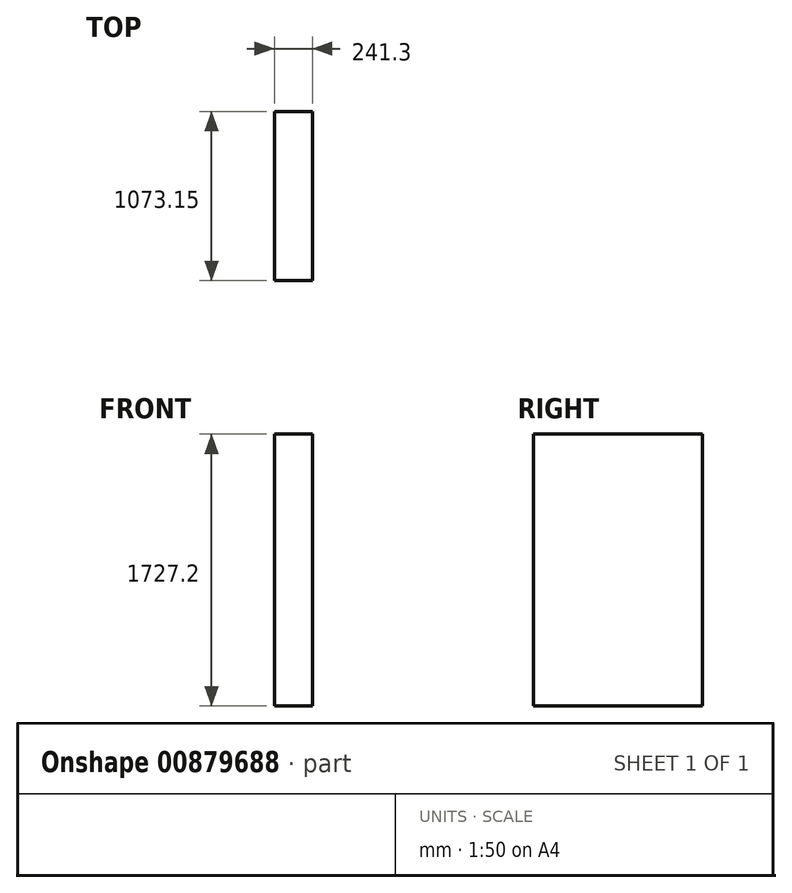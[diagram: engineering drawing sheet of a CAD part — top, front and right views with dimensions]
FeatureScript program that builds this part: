
annotation { "Feature Type Name" : "Feature", "Feature Type Description" : "" }
export const myFeature = defineFeature(function(context is Context, id is Id, definition is map)
    precondition{}
    {
        {
            var Q0;
            Q0=qCreatedBy(makeId("Top.planeOp"),FACE);
            var sketch = newSketch(context, id + "F0", { "sketchPlane" : qUnion([Q0])});
            skLineSegment(sketch, "E0.bottom", {"start": v(-119, -155.32) * mm, "end": v(122.3, -155.32) * mm});
            skLineSegment(sketch, "E0.top", {"start": v(-119, 917.83) * mm, "end": v(122.3, 917.83) * mm});
            skLineSegment(sketch, "E0.left", {"start": v(-119, -155.32) * mm, "end": v(-119, 917.83) * mm});
            skLineSegment(sketch, "E0.right", {"start": v(122.3, -155.32) * mm, "end": v(122.3, 917.83) * mm});
            skSolve(sketch);
        }
        {
            var Q0;
            Q0=makeQuery(id+"F0.imprint","IMPRINT",FACE,{"disambiguationData":[TD([[makeQuery(id+"F0.imprint","IMPRINT",EDGE,{"derivedFrom":sQuery(id+"F0.wireOp",EDGE,"E0.bottom")}),1.0]])]});
            extrude(context, id + "F1", {"entities" : qUnion([Q0]), "depth" : 1727.2 * mm, "offsetDistance" : 25.4 * mm});
        }
    });
